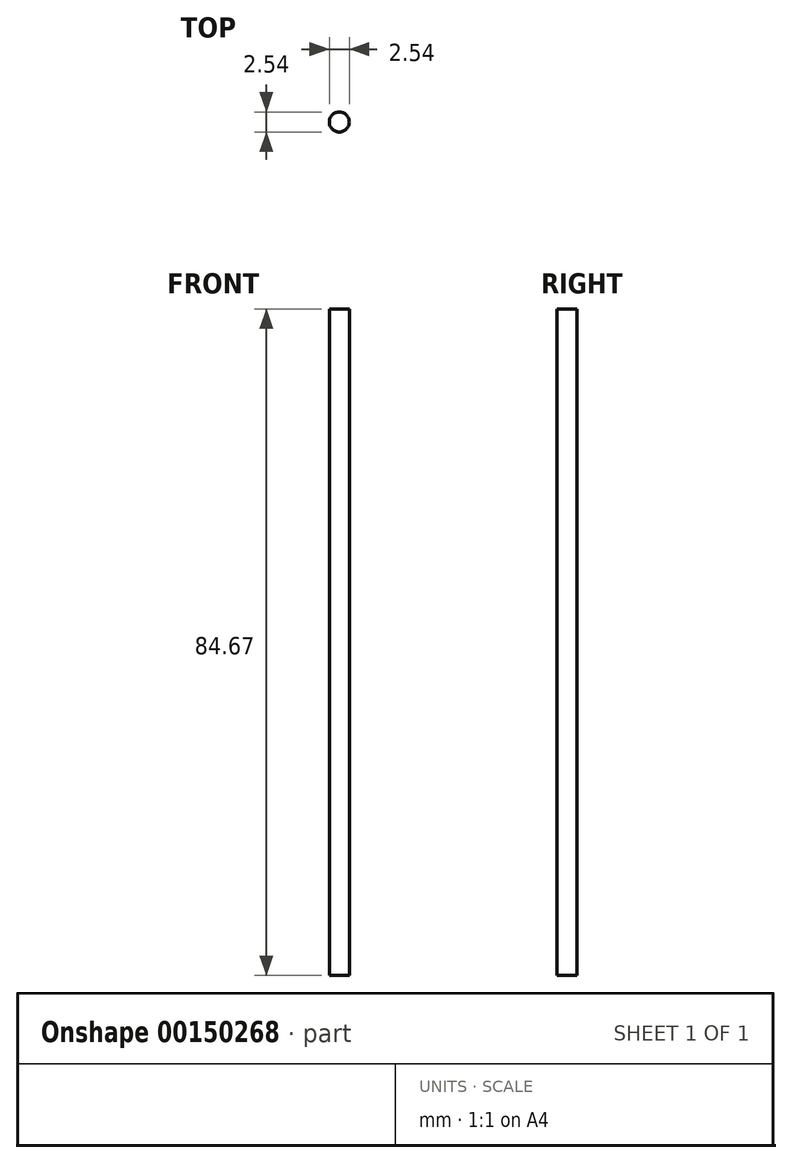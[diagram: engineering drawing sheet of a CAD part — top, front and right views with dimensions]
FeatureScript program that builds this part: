
annotation { "Feature Type Name" : "Feature", "Feature Type Description" : "" }
export const myFeature = defineFeature(function(context is Context, id is Id, definition is map)
    precondition{}
    {
        {
            var Q0;
            Q0=qCreatedBy(makeId("Top.planeOp"),FACE);
            var sketch = newSketch(context, id + "F0", { "sketchPlane" : qUnion([Q0])});
            skCircle(sketch, "E0", {"center": v(0, 0) * mm, "radius": 1.27 * mm});
            skSolve(sketch);
        }
        {
            var Q0;
            Q0=sQuery(id+"F0.wireOp",EDGE,"E0");
            extrude(context, id + "F1", {"bodyType" : ToolBodyType.SURFACE, "surfaceEntities" : qUnion([Q0]), "depth" : 84.67 * mm});
        }
    });
